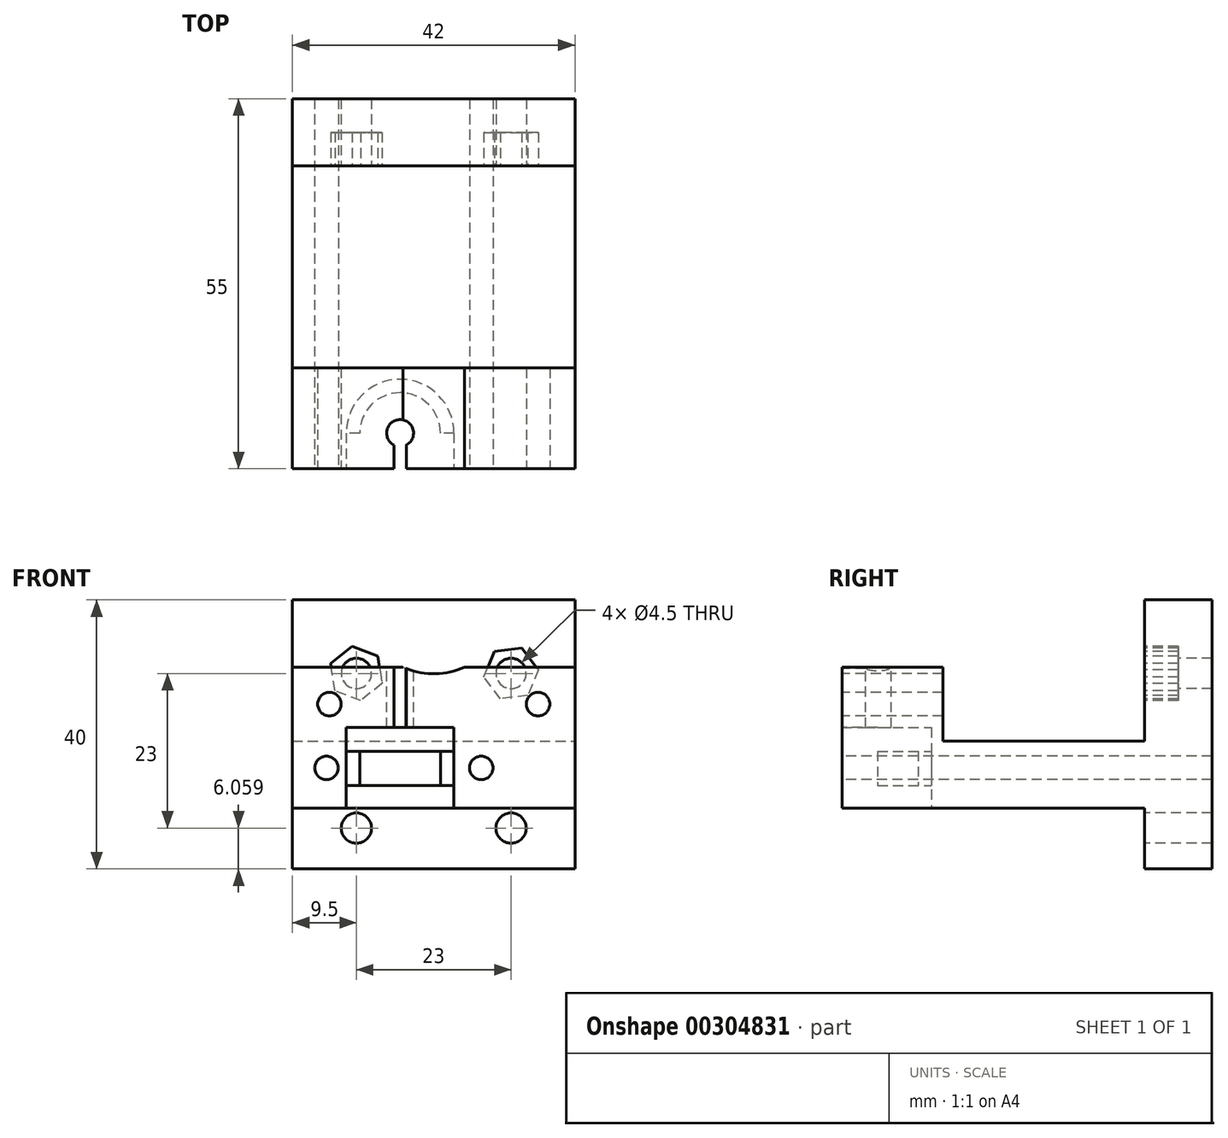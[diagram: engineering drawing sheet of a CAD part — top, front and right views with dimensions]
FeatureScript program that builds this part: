
annotation { "Feature Type Name" : "Feature", "Feature Type Description" : "" }
export const myFeature = defineFeature(function(context is Context, id is Id, definition is map)
    precondition{}
    {
        {
            var Q0;
            Q0=qCreatedBy(makeId("Front.planeOp"),FACE);
            var sketch = newSketch(context, id + "F0", { "sketchPlane" : qUnion([Q0])});
            skLineSegment(sketch, "E0.bottom", {"start": v(21, -21) * mm, "end": v(-21, -21) * mm});
            skPoint(sketch, "E0.middle", {"position": v(0, 0) * mm});
            skArc(sketch, "E1", {"start": v(-4.58, -10) * mm, "mid": v(0, -11) * mm, "end": v(4.58, -10) * mm});
            skLineSegment(sketch, "E2", {"start": v(-15.5, -11.63) * mm, "end": v(-15.5, 36) * mm, "construction": true});
            skLineSegment(sketch, "E3", {"start": v(-15.5, 36) * mm, "end": v(-15.5, -51.27) * mm, "construction": true});
            skPoint(sketch, "E4.endSnap0", {"position": v(0, -21) * mm});
            skCircle(sketch, "E5", {"center": v(15.5, -15.5) * mm, "radius": 1.75 * mm});
            skCircle(sketch, "E6", {"center": v(-15.5, -15.5) * mm, "radius": 1.75 * mm});
            skLineSegment(sketch, "E7", {"start": v(21, -10) * mm, "end": v(4.58, -10) * mm});
            skLineSegment(sketch, "E8", {"start": v(-21, -10) * mm, "end": v(-21, -21) * mm});
            skLineSegment(sketch, "E9", {"start": v(21, -10) * mm, "end": v(21, -21) * mm});
            skLineSegment(sketch, "E10.trimOffspring", {"start": v(-4.58, -10) * mm, "end": v(-21, -10) * mm});
            skSolve(sketch);
        }
        {
            var Q0;
            Q0=makeQuery(id+"F0.imprint","IMPRINT",FACE,{"disambiguationData":[TD([[makeQuery(id+"F0.imprint","IMPRINT",EDGE,{"derivedFrom":sQuery(id+"F0.wireOp",EDGE,"E0.bottom")}),-1.0]])]});
            extrude(context, id + "F1", {"entities" : qUnion([Q0]), "oppositeDirection" : true, "depth" : 15 * mm});
        }
        {
            var Q0;
            Q0=makeQuery(id+"F1.opExtrude","SWEPT_FACE",FACE,{"disambiguationData":[OSD([sQuery(id+"F0.wireOp",EDGE,"E0.bottom")])]});
            var sketch = newSketch(context, id + "F2", { "sketchPlane" : qUnion([Q0])});
            skLineSegment(sketch, "E11.bottom", {"start": v(-21, 0) * mm, "end": v(21, 0) * mm});
            skLineSegment(sketch, "E11.top", {"start": v(-21, -45) * mm, "end": v(21, -45) * mm});
            skLineSegment(sketch, "E11.left", {"start": v(-21, 0) * mm, "end": v(-21, -45) * mm});
            skLineSegment(sketch, "E11.right", {"start": v(21, 0) * mm, "end": v(21, -45) * mm});
            skLineSegment(sketch, "E12", {"start": v(-21, -15) * mm, "end": v(-21, -45) * mm, "construction": true});
            skSolve(sketch);
        }
        {
            var Q0;
            {var subQ0=sQuery(id+"F2.wireOp",EDGE,"E11.top");Q0=makeQuery(id+"F2.imprint","IMPRINT",FACE,{"disambiguationData":[TD([[makeQuery(id+"F2.imprint","IMPRINT",EDGE,{"derivedFrom":subQ0}),1.0]])]});}
            var Q1;
            Q1 = qSketchRegion(id + "F2", true);
            extrude(context, id + "F3", {"entities" : qUnion([Q0, Q1]), "operationType" : NewBodyOperationType.ADD, "depth" : 10 * mm});
        }
        {
            var Q0;
            Q0=makeQuery(id+"F3.opExtrude","SWEPT_FACE",FACE,{"disambiguationData":[OSD([sQuery(id+"F2.wireOp",EDGE,"E11.top")])]});
            var sketch = newSketch(context, id + "F4", { "sketchPlane" : qUnion([Q0])});
            skLineSegment(sketch, "E13.bottom", {"start": v(-21, 0) * mm, "end": v(21, 0) * mm});
            skLineSegment(sketch, "E13.top", {"start": v(-21, -40) * mm, "end": v(21, -40) * mm});
            skLineSegment(sketch, "E13.left", {"start": v(-21, 0) * mm, "end": v(-21, -40) * mm});
            skLineSegment(sketch, "E13.right", {"start": v(21, 0) * mm, "end": v(21, -40) * mm});
            skPoint(sketch, "E14.endSnap0", {"position": v(0, -19) * mm});
            skLineSegment(sketch, "E15.bottom", {"start": v(-11.5, -33.94) * mm, "end": v(11.5, -33.94) * mm, "construction": true});
            skLineSegment(sketch, "E15.top", {"start": v(-11.5, -10.94) * mm, "end": v(11.5, -10.94) * mm, "construction": true});
            skLineSegment(sketch, "E15.right", {"start": v(11.5, -33.94) * mm, "end": v(11.5, -10.94) * mm, "construction": true});
            skCircle(sketch, "E16", {"center": v(-11.5, -10.94) * mm, "radius": 2.25 * mm});
            skCircle(sketch, "E17", {"center": v(11.5, -10.94) * mm, "radius": 2.25 * mm});
            skCircle(sketch, "E18", {"center": v(-11.5, -33.94) * mm, "radius": 2.25 * mm});
            skCircle(sketch, "E19", {"center": v(11.5, -33.94) * mm, "radius": 2.25 * mm});
            skSolve(sketch);
        }
        {
            var Q0;
            Q0 = qSketchRegion(id + "F4", true);
            extrude(context, id + "F5", {"entities" : qUnion([Q0]), "operationType" : NewBodyOperationType.ADD, "depth" : 10 * mm});
        }
        {
            var Q0;
            Q0=makeQuery(id+"F1.opExtrude","SWEPT_FACE",FACE,{"disambiguationData":[OSD([sQuery(id+"F0.wireOp",EDGE,"E10.trimOffspring")])]});
            var sketch = newSketch(context, id + "F6", { "sketchPlane" : qUnion([Q0])});
            skLineSegment(sketch, "E20", {"start": v(-21, 7.5) * mm, "end": v(-5, 7.5) * mm, "construction": true});
            skLineSegment(sketch, "E21", {"start": v(-5, 15) * mm, "end": v(-5, 5.3) * mm, "construction": true});
            skCircle(sketch, "E22", {"center": v(-5, 5.3) * mm, "radius": 2 * mm});
            skSolve(sketch);
        }
        {
            var Q0;
            Q0 = qSketchRegion(id + "F6", true);
            extrude(context, id + "F7", {"entities" : qUnion([Q0]), "operationType" : NewBodyOperationType.REMOVE, "oppositeDirection" : true, "depth" : 25 * mm});
        }
        {
            var Q0;
            Q0=makeQuery(id+"F3.opExtrude","CAP_FACE",FACE,{"disambiguationData":[OSD([sQuery(id+"F2.wireOp",EDGE,"E11.bottom"),sQuery(id+"F2.wireOp",EDGE,"E11.top"),sQuery(id+"F2.wireOp",EDGE,"E11.left"),sQuery(id+"F2.wireOp",EDGE,"E11.right")])],"isStart":false});
            var sketch = newSketch(context, id + "F8", { "sketchPlane" : qUnion([Q0])});
            skCircle(sketch, "E23", {"center": v(-5, -5.3) * mm, "radius": 8 * mm});
            skSolve(sketch);
        }
        {
            var Q0;
            {var subQ0=sQuery(id+"F8.wireOp",EDGE,"E23");var subQ1=sQuery(id+"F2.wireOp",EDGE,"E11.bottom");var subQ2=makeQuery(id+"F3.opExtrude","CAP_EDGE",EDGE,{"disambiguationData":[OSD([subQ1])],"isStart":false});var subQ3=makeQuery(id+"F8.imprint","INTERSECT",VERTEX,{"disambiguationData":[OD(0.0)],"derivedFrom":[subQ2,subQ0]});Q0=makeQuery(id+"F8.imprint","IMPRINT",FACE,{"disambiguationData":[TD([[makeQuery(id+"F8.imprint","IMPRINT",EDGE,{"disambiguationData":[TD([[subQ3,1.0]])],"derivedFrom":subQ0}),1.0]])]});}
            var Q1;
            Q1=sQuery(id+"F8.wireOp",EDGE,"E23");
            extrude(context, id + "F9", {"entities" : qUnion([Q0]), "operationType" : NewBodyOperationType.REMOVE, "surfaceEntities" : qUnion([Q1]), "oppositeDirection" : true, "depth" : 12 * mm});
        }
        {
            var Q0;
            Q0=makeQuery(id+"F3.opExtrude","CAP_FACE",FACE,{"disambiguationData":[OSD([sQuery(id+"F2.wireOp",EDGE,"E11.bottom"),sQuery(id+"F2.wireOp",EDGE,"E11.top"),sQuery(id+"F2.wireOp",EDGE,"E11.left"),sQuery(id+"F2.wireOp",EDGE,"E11.right")])],"isStart":false});
            var sketch = newSketch(context, id + "F10", { "sketchPlane" : qUnion([Q0])});
            skCircle(sketch, "E24", {"center": v(-5, -5.3) * mm, "radius": 8 * mm});
            skSolve(sketch);
        }
        {
            var Q0;
            {var subQ0=sQuery(id+"F10.wireOp",EDGE,"E24");var subQ3=sQuery(id+"F2.wireOp",EDGE,"E11.bottom");var subQ6=sQuery(id+"F0.wireOp",EDGE,"E9");var subQ10=makeQuery(id+"F3.opExtrude","CAP_EDGE",EDGE,{"disambiguationData":[OSD([subQ3])],"isStart":false});var subQ11=makeQuery(id+"F10.imprint","INTERSECT",VERTEX,{"derivedFrom":[makeQuery(id+"F9.boolean.opBoolean","SPLIT",EDGE,{"disambiguationData":[TD([makeQuery(id+"F1.opExtrude","SWEPT_FACE",FACE,{"disambiguationData":[OSD([subQ6])]})])],"derivedFrom":subQ10}),subQ0]});Q0=makeQuery(id+"F10.imprint","IMPRINT",FACE,{"disambiguationData":[TD([[makeQuery(id+"F10.imprint","IMPRINT",EDGE,{"disambiguationData":[TD([[subQ11,-1.0]])],"derivedFrom":subQ0}),1.0]])]});}
            var Q1;
            Q1=sQuery(id+"F10.wireOp",EDGE,"E24");
            extrude(context, id + "F11", {"entities" : qUnion([Q0]), "surfaceEntities" : qUnion([Q1]), "oppositeDirection" : true, "depth" : 8.5 * mm});
        }
        {
            var Q0;
            Q0=makeQuery(id+"F11.opExtrude","CAP_FACE",FACE,{"disambiguationData":[OSD([sQuery(id+"F10.wireOp",EDGE,"E24")])],"isStart":true});
            var sketch = newSketch(context, id + "F12", { "sketchPlane" : qUnion([Q0])});
            skCircle(sketch, "E25", {"center": v(-5, -5.3) * mm, "radius": 6 * mm});
            skSolve(sketch);
        }
        {
            var Q0;
            Q0=makeQuery(id+"F12.imprint","IMPRINT",FACE,{"disambiguationData":[TD([[makeQuery(id+"F12.imprint","IMPRINT",EDGE,{"derivedFrom":sQuery(id+"F12.wireOp",EDGE,"E25")}),1.0]])]});
            var Q1;
            Q1=sQuery(id+"F12.wireOp",EDGE,"E25");
            extrude(context, id + "F13", {"entities" : qUnion([Q0]), "operationType" : NewBodyOperationType.REMOVE, "surfaceEntities" : qUnion([Q1]), "oppositeDirection" : true, "offsetDistance" : 25 * mm, "depth" : 9 * mm});
        }
        {
            var Q0;
            Q0=makeQuery(id+"F11.opExtrude","CAP_FACE",FACE,{"disambiguationData":[OSD([sQuery(id+"F10.wireOp",EDGE,"E24")])],"isStart":true});
            var sketch = newSketch(context, id + "F14", { "sketchPlane" : qUnion([Q0])});
            skCircle(sketch, "E26", {"center": v(-5, -5.3) * mm, "radius": 8 * mm});
            skSolve(sketch);
        }
        {
            var Q0;
            Q0 = qSketchRegion(id + "F14", true);
            extrude(context, id + "F15", {"entities" : qUnion([Q0]), "operationType" : NewBodyOperationType.REMOVE, "oppositeDirection" : true, "depth" : 3.4 * mm});
        }
        {
            var Q0;
            Q0=makeQuery(id+"F3.opExtrude","CAP_FACE",FACE,{"disambiguationData":[OSD([sQuery(id+"F2.wireOp",EDGE,"E11.bottom"),sQuery(id+"F2.wireOp",EDGE,"E11.top"),sQuery(id+"F2.wireOp",EDGE,"E11.left"),sQuery(id+"F2.wireOp",EDGE,"E11.right")])],"isStart":false});
            var sketch = newSketch(context, id + "F16", { "sketchPlane" : qUnion([Q0])});
            skLineSegment(sketch, "E27", {"start": v(-5, -5.3) * mm, "end": v(-5, -13.3) * mm, "construction": true});
            skPoint(sketch, "E27.endSnap0", {"position": v(-5, -13.3) * mm});
            skLineSegment(sketch, "E28", {"start": v(-5, -13.3) * mm, "end": v(3, -13.3) * mm, "construction": true});
            skLineSegment(sketch, "E29", {"start": v(3, -13.3) * mm, "end": v(7.22, -13.3) * mm, "construction": true});
            skLineSegment(sketch, "E30.bottom", {"start": v(3, -5.3) * mm, "end": v(-13, -5.3) * mm});
            skLineSegment(sketch, "E30.top", {"start": v(3, 3.31) * mm, "end": v(-13, 3.31) * mm});
            skLineSegment(sketch, "E30.left", {"start": v(3, -5.3) * mm, "end": v(3, 3.31) * mm});
            skLineSegment(sketch, "E30.right", {"start": v(-13, -5.3) * mm, "end": v(-13, 3.31) * mm});
            skSolve(sketch);
        }
        {
            var Q0;
            Q0 = qSketchRegion(id + "F16", true);
            extrude(context, id + "F17", {"entities" : qUnion([Q0]), "operationType" : NewBodyOperationType.REMOVE, "oppositeDirection" : true, "depth" : 12 * mm});
        }
        {
            var Q0;
            Q0=makeQuery(id+"F3.boolean.opBoolean","MERGE",FACE,{"derivedFrom":[makeQuery(id+"F1.opExtrude","CAP_FACE",FACE,{"disambiguationData":[OSD([sQuery(id+"F0.wireOp",EDGE,"E0.bottom"),sQuery(id+"F0.wireOp",EDGE,"E1"),sQuery(id+"F0.wireOp",EDGE,"E5"),sQuery(id+"F0.wireOp",EDGE,"E6"),sQuery(id+"F0.wireOp",EDGE,"E7"),sQuery(id+"F0.wireOp",EDGE,"E8"),sQuery(id+"F0.wireOp",EDGE,"E9"),sQuery(id+"F0.wireOp",EDGE,"E10.trimOffspring")])],"isStart":true}),makeQuery(id+"F3.opExtrude","SWEPT_FACE",FACE,{"disambiguationData":[OSD([sQuery(id+"F2.wireOp",EDGE,"E11.bottom")])]})]});
            var sketch = newSketch(context, id + "F18", { "sketchPlane" : qUnion([Q0])});
            skLineSegment(sketch, "E31", {"start": v(7.06, -25) * mm, "end": v(7.06, -22.6) * mm, "construction": true});
            skCircle(sketch, "E32", {"center": v(-15.94, -25) * mm, "radius": 1.75 * mm});
            skCircle(sketch, "E33", {"center": v(7.06, -25) * mm, "radius": 1.75 * mm});
            skSolve(sketch);
        }
        {
            var Q0;
            Q0 = qSketchRegion(id + "F18", true);
            extrude(context, id + "F19", {"entities" : qUnion([Q0]), "operationType" : NewBodyOperationType.REMOVE, "oppositeDirection" : true, "depth" : 55 * mm});
        }
        {
            var Q0;
            {var subQ2=sQuery(id+"F4.wireOp",EDGE,"E17");var subQ3=sQuery(id+"F4.wireOp",EDGE,"E13.bottom");var subQ4=sQuery(id+"F4.wireOp",EDGE,"E13.left");var subQ5=sQuery(id+"F4.wireOp",EDGE,"E13.right");var subQ6=sQuery(id+"F4.wireOp",EDGE,"E16");Q0=makeQuery(id+"F5.boolean.opBoolean","SPLIT",FACE,{"disambiguationData":[TD([makeQuery(id+"F5.opExtrude","SWEPT_FACE",FACE,{"disambiguationData":[OSD([subQ3])]})])],"derivedFrom":makeQuery(id+"F5.opExtrude","CAP_FACE",FACE,{"disambiguationData":[OSD([subQ3,sQuery(id+"F4.wireOp",EDGE,"E13.top"),subQ4,subQ5,subQ6,subQ2,sQuery(id+"F4.wireOp",EDGE,"E18"),sQuery(id+"F4.wireOp",EDGE,"E19")])],"isStart":true})});}
            var sketch = newSketch(context, id + "F20", { "sketchPlane" : qUnion([Q0])});
            skCircle(sketch, "E34.cCircle", {"center": v(-11.5, -10.94) * mm, "radius": 4.1 * mm, "construction": true});
            skLineSegment(sketch, "E34.0", {"start": v(-7.67, -12.41) * mm, "end": v(-10.86, -15) * mm});
            skLineSegment(sketch, "E34.1", {"start": v(-10.86, -15) * mm, "end": v(-14.69, -13.52) * mm});
            skLineSegment(sketch, "E34.2", {"start": v(-14.69, -13.52) * mm, "end": v(-15.33, -9.47) * mm});
            skLineSegment(sketch, "E34.3", {"start": v(-15.33, -9.47) * mm, "end": v(-12.14, -6.9) * mm});
            skLineSegment(sketch, "E34.4", {"start": v(-12.14, -6.9) * mm, "end": v(-8.31, -8.36) * mm});
            skLineSegment(sketch, "E34.5", {"start": v(-8.31, -8.36) * mm, "end": v(-7.67, -12.41) * mm});
            skCircle(sketch, "E35.cCircle", {"center": v(11.5, -10.94) * mm, "radius": 4.1 * mm, "construction": true});
            skLineSegment(sketch, "E35.0", {"start": v(13.98, -14.2) * mm, "end": v(9.92, -14.72) * mm});
            skLineSegment(sketch, "E35.1", {"start": v(9.92, -14.72) * mm, "end": v(7.43, -11.46) * mm});
            skLineSegment(sketch, "E35.2", {"start": v(7.43, -11.46) * mm, "end": v(9.02, -7.68) * mm});
            skLineSegment(sketch, "E35.3", {"start": v(9.02, -7.68) * mm, "end": v(13.08, -7.16) * mm});
            skLineSegment(sketch, "E35.4", {"start": v(13.08, -7.16) * mm, "end": v(15.57, -10.42) * mm});
            skLineSegment(sketch, "E35.5", {"start": v(15.57, -10.42) * mm, "end": v(13.98, -14.2) * mm});
            skSolve(sketch);
        }
        {
            var Q0;
            Q0 = qSketchRegion(id + "F20", true);
            extrude(context, id + "F21", {"entities" : qUnion([Q0]), "operationType" : NewBodyOperationType.REMOVE, "oppositeDirection" : true, "depth" : 5 * mm});
        }
        {
            var Q0;
            Q0=makeQuery(id+"F1.opExtrude","SWEPT_FACE",FACE,{"disambiguationData":[OSD([sQuery(id+"F0.wireOp",EDGE,"E10.trimOffspring")])]});
            var sketch = newSketch(context, id + "F22", { "sketchPlane" : qUnion([Q0])});
            skLineSegment(sketch, "E36.bottom", {"start": v(-5.87, 3.5) * mm, "end": v(-4.07, 3.5) * mm});
            skLineSegment(sketch, "E36.top", {"start": v(-5.87, 0) * mm, "end": v(-4.07, 0) * mm});
            skLineSegment(sketch, "E36.left", {"start": v(-5.87, 3.5) * mm, "end": v(-5.87, 0) * mm});
            skLineSegment(sketch, "E36.right", {"start": v(-4.07, 3.5) * mm, "end": v(-4.07, 0) * mm});
            skSolve(sketch);
        }
        {
            var Q0;
            Q0 = qSketchRegion(id + "F22", true);
            extrude(context, id + "F23", {"entities" : qUnion([Q0]), "operationType" : NewBodyOperationType.REMOVE, "oppositeDirection" : true, "depth" : 25 * mm});
        }
    });
